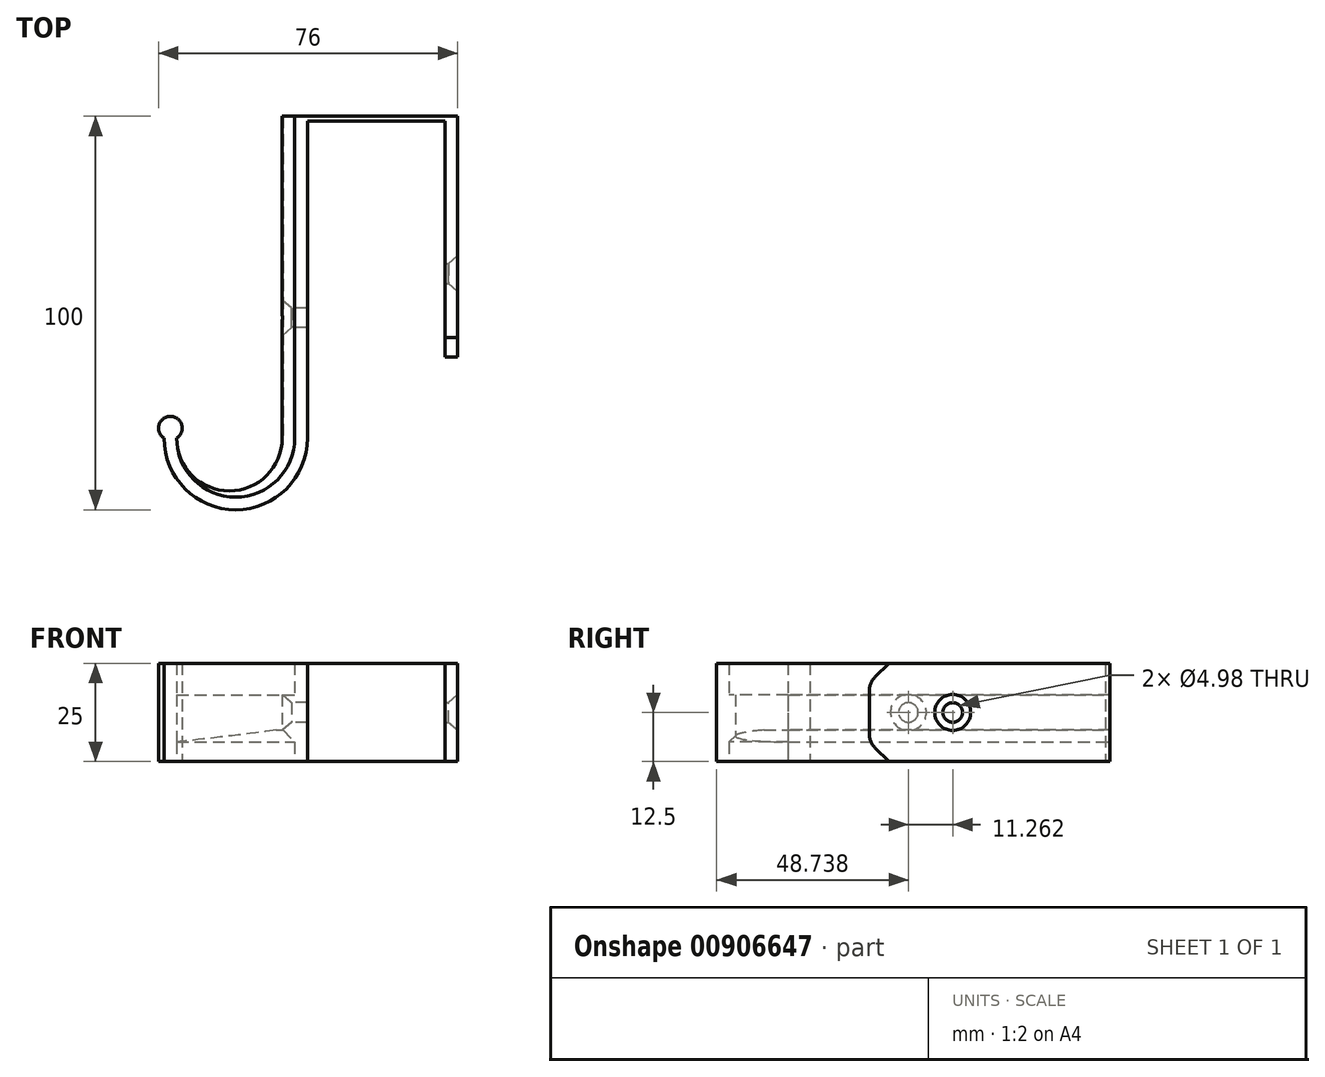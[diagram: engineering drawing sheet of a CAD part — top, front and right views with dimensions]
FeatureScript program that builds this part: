
annotation { "Feature Type Name" : "Feature", "Feature Type Description" : "" }
export const myFeature = defineFeature(function(context is Context, id is Id, definition is map)
    precondition{}
    {
        {
            var Q0;
            Q0=qCreatedBy(makeId("Top.planeOp"),FACE);
            var sketch = newSketch(context, id + "F0", { "sketchPlane" : qUnion([Q0])});
            skLineSegment(sketch, "E0.bottom", {"start": v(-58.42, 58.42) * mm, "end": v(58.42, 58.42) * mm, "construction": true});
            skLineSegment(sketch, "E0.top", {"start": v(-58.42, -58.42) * mm, "end": v(58.42, -58.42) * mm, "construction": true});
            skLineSegment(sketch, "E0.left", {"start": v(-58.42, 58.42) * mm, "end": v(-58.42, -58.42) * mm, "construction": true});
            skLineSegment(sketch, "E0.right", {"start": v(58.42, 58.42) * mm, "end": v(58.42, -58.42) * mm, "construction": true});
            skPoint(sketch, "E0.middle", {"position": v(0, 0) * mm});
            skLineSegment(sketch, "E1", {"start": v(38, -11.2) * mm, "end": v(38, 50) * mm});
            skLineSegment(sketch, "E2", {"start": v(38, 50) * mm, "end": v(-3.4, 50) * mm});
            skLineSegment(sketch, "E3", {"start": v(-3.4, 50) * mm, "end": v(-3.4, -31.8) * mm});
            skArc(sketch, "E4", {"start": v(-33.4, -31.8) * mm, "mid": v(-18.4, -46.8) * mm, "end": v(-3.4, -31.8) * mm});
            skLineSegment(sketch, "E5", {"start": v(38, -11.2) * mm, "end": v(34.8, -11.2) * mm});
            skLineSegment(sketch, "E6", {"start": v(34.8, -11.2) * mm, "end": v(34.8, 48.8) * mm});
            skLineSegment(sketch, "E7", {"start": v(34.8, 48.8) * mm, "end": v(-0.2, 48.8) * mm});
            skLineSegment(sketch, "E8", {"start": v(-0.2, 48.8) * mm, "end": v(-0.2, -31.8) * mm});
            skArc(sketch, "E9", {"start": v(-36.6, -31.8) * mm, "mid": v(-18.4, -50) * mm, "end": v(-0.2, -31.8) * mm});
            skArc(sketch, "E10", {"start": v(-33.4, -31.8) * mm, "mid": v(-35, -26.26) * mm, "end": v(-36.6, -31.8) * mm});
            skLineSegment(sketch, "E11.bottom", {"start": v(-38, 50) * mm, "end": v(38, 50) * mm, "construction": true});
            skLineSegment(sketch, "E11.top", {"start": v(-38, -50) * mm, "end": v(38, -50) * mm, "construction": true});
            skLineSegment(sketch, "E11.left", {"start": v(-38, 50) * mm, "end": v(-38, -50) * mm, "construction": true});
            skLineSegment(sketch, "E11.right", {"start": v(38, 50) * mm, "end": v(38, -50) * mm, "construction": true});
            skArc(sketch, "E12", {"start": v(-33.4, -31.8) * mm, "mid": v(-20, -45.2) * mm, "end": v(-6.6, -31.8) * mm});
            skLineSegment(sketch, "E13", {"start": v(-6.6, -31.8) * mm, "end": v(-6.6, 50) * mm});
            skLineSegment(sketch, "E14", {"start": v(-6.6, 50) * mm, "end": v(-3.4, 50) * mm});
            skSolve(sketch);
        }
        {
            var Q0;
            Q0=makeQuery(id+"F0.imprint","IMPRINT",FACE,{"disambiguationData":[TD([[makeQuery(id+"F0.imprint","IMPRINT",EDGE,{"derivedFrom":sQuery(id+"F0.wireOp",EDGE,"E1")}),1.0]])]});
            extrude(context, id + "F1", {"entities" : qUnion([Q0]), "endBound" : BoundingType.SYMMETRIC, "depth" : 25 * mm, "offsetDistance" : 25 * mm});
        }
        {
            var Q0;
            Q0=makeQuery(id+"F0.imprint","IMPRINT",FACE,{"disambiguationData":[TD([[makeQuery(id+"F0.imprint","IMPRINT",EDGE,{"derivedFrom":sQuery(id+"F0.wireOp",EDGE,"E3")}),-1.0]])]});
            extrude(context, id + "F2", {"entities" : qUnion([Q0]), "operationType" : NewBodyOperationType.ADD, "endBound" : BoundingType.SYMMETRIC, "depth" : 9 * mm, "offsetDistance" : 25 * mm});
        }
        {
            var Q0;
            Q0=makeQuery(id+"F2.opExtrude","CAP_EDGE",EDGE,{"disambiguationData":[OSD([sQuery(id+"F0.wireOp",EDGE,"E3")])],"isStart":false});
            var Q1;
            Q1=makeQuery(id+"F2.opExtrude","CAP_EDGE",EDGE,{"disambiguationData":[OSD([sQuery(id+"F0.wireOp",EDGE,"E3")])],"isStart":true});
            chamfer(context, id + "F3", {"entities" : qUnion([Q0, Q1]), "width" : 3 * mm, "tangentPropagation" : true});
        }
        {
            var Q0;
            Q0=makeQuery(id+"F1.opExtrude","CAP_EDGE",EDGE,{"disambiguationData":[OSD([sQuery(id+"F0.wireOp",EDGE,"E5")])],"isStart":false});
            var Q1;
            Q1=makeQuery(id+"F1.opExtrude","CAP_EDGE",EDGE,{"disambiguationData":[OSD([sQuery(id+"F0.wireOp",EDGE,"E5")])],"isStart":true});
            chamfer(context, id + "F4", {"entities" : qUnion([Q0, Q1]), "width" : 5 * mm, "tangentPropagation" : true});
        }
        {
            var Q0;
            {var subQ0=sQuery(id+"F0.wireOp",EDGE,"E5");Q0=makeQuery(id+"F4.opChamfer","BLEND_EDGE",EDGE,{"blendedFrom":[makeQuery(id+"F1.opExtrude","CAP_EDGE",EDGE,{"disambiguationData":[OSD([subQ0])],"isStart":true}),makeQuery(id+"F1.opExtrude","SWEPT_FACE",FACE,{"disambiguationData":[OSD([subQ0])]})],"blendedInto":[makeQuery(id+"F1.opExtrude","SWEPT_FACE",FACE,{"disambiguationData":[OSD([subQ0])]})]});}
            var Q1;
            {var subQ0=sQuery(id+"F0.wireOp",EDGE,"E5");Q1=makeQuery(id+"F4.opChamfer","BLEND_EDGE",EDGE,{"blendedFrom":[makeQuery(id+"F1.opExtrude","CAP_EDGE",EDGE,{"disambiguationData":[OSD([subQ0])],"isStart":false}),makeQuery(id+"F1.opExtrude","SWEPT_FACE",FACE,{"disambiguationData":[OSD([subQ0])]})],"blendedInto":[makeQuery(id+"F1.opExtrude","SWEPT_FACE",FACE,{"disambiguationData":[OSD([subQ0])]})]});}
            fillet(context, id + "F5", {"entities" : qUnion([Q0, Q1]), "radius" : 5 * mm, "tangentPropagation" : true, "allowEdgeOverflow" : false});
        }
        {
            var Q0;
            Q0=makeQuery(id+"F2.opExtrude","SWEPT_FACE",FACE,{"disambiguationData":[OSD([sQuery(id+"F0.wireOp",EDGE,"E13")])]});
            var sketch = newSketch(context, id + "F6", { "sketchPlane" : qUnion([Q0])});
            skPoint(sketch, "E15", {"position": v(1.26, 0) * mm});
            skSolve(sketch);
        }
        {
            var Q0;
            Q0=sQuery(id+"F6.wireOp",VERTEX,"E15");
            var Q1;
            Q1=makeQuery(id+"F1.opExtrude","SWEPT_BODY",BODY,{"disambiguationData":[OSD([sQuery(id+"F0.wireOp",EDGE,"E1"),sQuery(id+"F0.wireOp",EDGE,"E2"),sQuery(id+"F0.wireOp",EDGE,"E3"),sQuery(id+"F0.wireOp",EDGE,"E4"),sQuery(id+"F0.wireOp",EDGE,"E5"),sQuery(id+"F0.wireOp",EDGE,"E6"),sQuery(id+"F0.wireOp",EDGE,"E7"),sQuery(id+"F0.wireOp",EDGE,"E8"),sQuery(id+"F0.wireOp",EDGE,"E9"),sQuery(id+"F0.wireOp",EDGE,"E10")])]});
            hole(context, id + "F7", {"style" : HoleStyle.C_SINK, "endStyle" : HoleEndStyle.BLIND, "standardTappedOrClearance" : lookupTablePath({ "fit" : "Normal (ASME)", "standard" : "ANSI", "size" : "#8", "type" : "Clearance" }), "standardBlindInLast" : lookupTablePath({ "fit" : "Normal", "standard" : "ANSI", "size" : "#8", "type" : "Clearance" }), "holeDiameter" : 4.98 * mm, "cSinkDiameter" : 9.12 * mm, "cSinkAngle" : 82 * degree, "majorDiameter" : 5 * mm, "holeDepth" : 10 * mm, "isTappedThrough" : true, "tappedDepth" : 12 * mm, "tapClearance" : 3, "startFromSketch" : true, "locations" : qUnion([Q0]), "scope" : qUnion([Q1])});
        }
        {
            var Q0;
            Q0=makeQuery(id+"F1.opExtrude","SWEPT_FACE",FACE,{"disambiguationData":[OSD([sQuery(id+"F0.wireOp",EDGE,"E1")])]});
            var sketch = newSketch(context, id + "F8", { "sketchPlane" : qUnion([Q0])});
            skPoint(sketch, "E16", {"position": v(10, 0) * mm});
            skSolve(sketch);
        }
        {
            var Q0;
            Q0=sQuery(id+"F8.wireOp",VERTEX,"E16");
            var Q1;
            Q1=makeQuery(id+"F1.opExtrude","SWEPT_BODY",BODY,{"disambiguationData":[OSD([sQuery(id+"F0.wireOp",EDGE,"E1"),sQuery(id+"F0.wireOp",EDGE,"E2"),sQuery(id+"F0.wireOp",EDGE,"E3"),sQuery(id+"F0.wireOp",EDGE,"E4"),sQuery(id+"F0.wireOp",EDGE,"E5"),sQuery(id+"F0.wireOp",EDGE,"E6"),sQuery(id+"F0.wireOp",EDGE,"E7"),sQuery(id+"F0.wireOp",EDGE,"E8"),sQuery(id+"F0.wireOp",EDGE,"E9"),sQuery(id+"F0.wireOp",EDGE,"E10")])]});
            hole(context, id + "F9", {"style" : HoleStyle.C_SINK, "endStyle" : HoleEndStyle.BLIND, "standardTappedOrClearance" : lookupTablePath({ "fit" : "Normal (ASME)", "standard" : "ANSI", "size" : "#8", "type" : "Clearance" }), "standardBlindInLast" : lookupTablePath({ "fit" : "Normal", "standard" : "ANSI", "size" : "#8", "type" : "Clearance" }), "holeDiameter" : 4.98 * mm, "cSinkDiameter" : 9.12 * mm, "cSinkAngle" : 82 * degree, "majorDiameter" : 5 * mm, "holeDepth" : 10 * mm, "isTappedThrough" : true, "tappedDepth" : 12 * mm, "tapClearance" : 3, "startFromSketch" : true, "locations" : qUnion([Q0]), "scope" : qUnion([Q1])});
        }
    });
